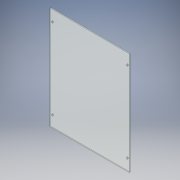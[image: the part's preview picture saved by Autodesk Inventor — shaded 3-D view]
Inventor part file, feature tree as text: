
AUTODESK INVENTOR PART (.ipt)
format: ipt  version: 2019 (Build 230136000, 136)  size: 113,152 bytes
history: native  units: mm
features: extrude x2, sketch x2
ambient origin geometry x8: Origin, YZ Plane, XZ Plane, XY Plane, X Axis, Y Axis, Z Axis, Center Point
bodies: Solid1 (feature_tree)
feature tree (4):
  extrude  "Extrusion1"  Depth=460.0mm
  extrude  "Extrusion2"  Depth=4.0mm
  sketch  "Sketch1"  dims[d0=354.0mm d1=460.0mm]
  sketch  "Sketch2"  dims[d2=4.0mm d3=0.0mm d4=8.0mm d5=8.0mm d6=8.0mm d7=8.0mm d8=50.0mm d9=9.5mm d10=50.0mm d11=9.5mm d12=50.0mm d13=9.5mm d14=50.0mm d15=9.5mm d16=4.0mm d17=0.0mm]
